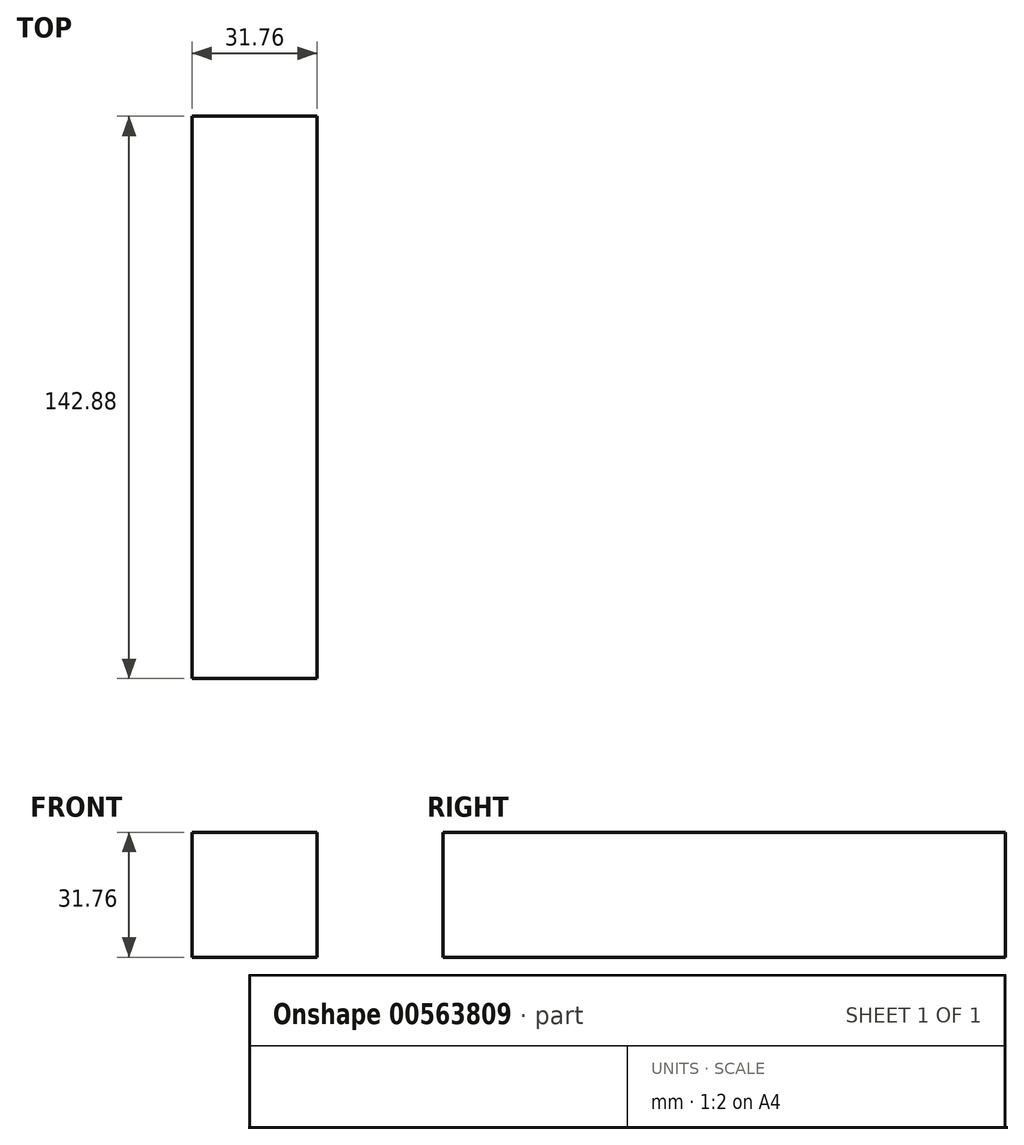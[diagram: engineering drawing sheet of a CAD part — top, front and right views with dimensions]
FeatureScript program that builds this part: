
annotation { "Feature Type Name" : "Feature", "Feature Type Description" : "" }
export const myFeature = defineFeature(function(context is Context, id is Id, definition is map)
    precondition{}
    {
        {
            var Q0;
            Q0=qCreatedBy(makeId("Front.planeOp"),FACE);
            var sketch = newSketch(context, id + "F0", { "sketchPlane" : qUnion([Q0])});
            skLineSegment(sketch, "E0.bottom", {"start": v(-15.87, 15.88) * mm, "end": v(15.88, 15.88) * mm});
            skLineSegment(sketch, "E0.top", {"start": v(-15.88, -15.88) * mm, "end": v(15.87, -15.88) * mm});
            skLineSegment(sketch, "E0.left", {"start": v(-15.87, 15.88) * mm, "end": v(-15.88, -15.88) * mm});
            skLineSegment(sketch, "E0.right", {"start": v(15.88, 15.88) * mm, "end": v(15.87, -15.88) * mm});
            skPoint(sketch, "E0.middle", {"position": v(0, 0) * mm});
            skSolve(sketch);
        }
        {
            var Q0;
            Q0=makeQuery(id+"F0.imprint","IMPRINT",FACE,{"disambiguationData":[TD([[makeQuery(id+"F0.imprint","IMPRINT",EDGE,{"derivedFrom":sQuery(id+"F0.wireOp",EDGE,"E0.bottom")}),-1.0]])]});
            extrude(context, id + "F1", {"entities" : qUnion([Q0]), "endBound" : BoundingType.SYMMETRIC, "depth" : 142.88 * mm, "offsetDistance" : 25.4 * mm});
        }
    });
